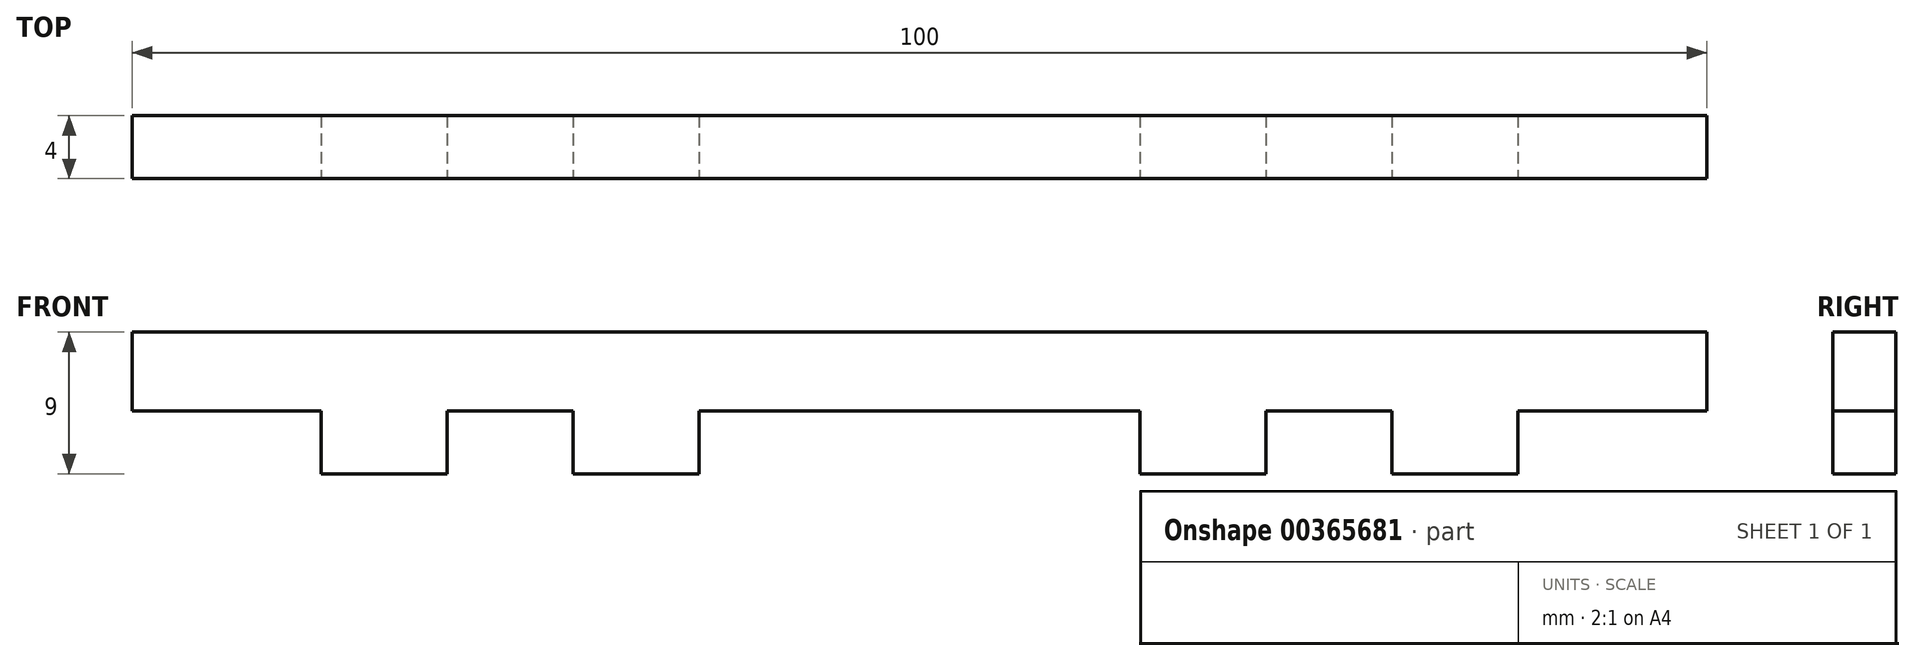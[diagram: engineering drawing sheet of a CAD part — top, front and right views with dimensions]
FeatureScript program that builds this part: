
annotation { "Feature Type Name" : "Feature", "Feature Type Description" : "" }
export const myFeature = defineFeature(function(context is Context, id is Id, definition is map)
    precondition{}
    {
        {
            var Q0;
            Q0=qCreatedBy(makeId("Front.planeOp"),FACE);
            var sketch = newSketch(context, id + "F0", { "sketchPlane" : qUnion([Q0])});
            skLineSegment(sketch, "E0.bottom", {"start": v(0, 0) * mm, "end": v(100, 0) * mm});
            skLineSegment(sketch, "E0.top", {"start": v(0, 5) * mm, "end": v(100, 5) * mm});
            skLineSegment(sketch, "E0.left", {"start": v(0, 0) * mm, "end": v(0, 5) * mm});
            skLineSegment(sketch, "E0.right", {"start": v(100, 0) * mm, "end": v(100, 5) * mm});
            skSolve(sketch);
        }
        {
            var Q0;
            Q0 = qSketchRegion(id + "F0", true);
            extrude(context, id + "F1", {"entities" : qUnion([Q0]), "depth" : 4 * mm});
        }
        {
            var Q0;
            Q0=makeQuery(id+"F1.opExtrude","CAP_FACE",FACE,{"disambiguationData":[OSD([sQuery(id+"F0.wireOp",EDGE,"E0.bottom"),sQuery(id+"F0.wireOp",EDGE,"E0.top"),sQuery(id+"F0.wireOp",EDGE,"E0.left"),sQuery(id+"F0.wireOp",EDGE,"E0.right")])],"isStart":false});
            var sketch = newSketch(context, id + "F2", { "sketchPlane" : qUnion([Q0])});
            skLineSegment(sketch, "E1.bottom", {"start": v(12, 0) * mm, "end": v(20, 0) * mm});
            skLineSegment(sketch, "E1.top", {"start": v(12, -4) * mm, "end": v(20, -4) * mm});
            skLineSegment(sketch, "E1.left", {"start": v(12, 0) * mm, "end": v(12, -4) * mm});
            skLineSegment(sketch, "E1.right", {"start": v(20, 0) * mm, "end": v(20, -4) * mm});
            skLineSegment(sketch, "E2.1.0.0", {"start": v(28, 0) * mm, "end": v(36, 0) * mm});
            skLineSegment(sketch, "E2.1.0.1", {"start": v(28, -4) * mm, "end": v(36, -4) * mm});
            skLineSegment(sketch, "E2.1.0.2", {"start": v(28, 0) * mm, "end": v(28, -4) * mm});
            skLineSegment(sketch, "E2.1.0.3", {"start": v(36, 0) * mm, "end": v(36, -4) * mm});
            skLineSegment(sketch, "E2.direction1", {"start": v(12, -4) * mm, "end": v(28, -4) * mm, "construction": true});
            skLineSegment(sketch, "E3", {"start": v(50, 5) * mm, "end": v(50, 0) * mm, "construction": true});
            skLineSegment(sketch, "E4.MirrorCS", {"start": v(88, -4) * mm, "end": v(80, -4) * mm});
            skLineSegment(sketch, "E5.MirrorCS", {"start": v(64, 0) * mm, "end": v(64, -4) * mm});
            skLineSegment(sketch, "E6.MirrorCS", {"start": v(88, -4) * mm, "end": v(72, -4) * mm, "construction": true});
            skLineSegment(sketch, "E7.MirrorCS", {"start": v(72, 0) * mm, "end": v(72, -4) * mm});
            skLineSegment(sketch, "E8.MirrorCS", {"start": v(72, -4) * mm, "end": v(64, -4) * mm});
            skLineSegment(sketch, "E9.MirrorCS", {"start": v(72, 0) * mm, "end": v(64, 0) * mm});
            skLineSegment(sketch, "E10.MirrorCS", {"start": v(80, 0) * mm, "end": v(80, -4) * mm});
            skLineSegment(sketch, "E11.MirrorCS", {"start": v(88, 0) * mm, "end": v(88, -4) * mm});
            skLineSegment(sketch, "E12.MirrorCS", {"start": v(88, 0) * mm, "end": v(80, 0) * mm});
            skSolve(sketch);
        }
        {
            var Q0;
            Q0 = qSketchRegion(id + "F2", true);
            extrude(context, id + "F3", {"entities" : qUnion([Q0]), "operationType" : NewBodyOperationType.ADD, "oppositeDirection" : true, "depth" : 4 * mm});
        }
    });
